# Revit family: 46-PORTARROLLOS METÁLICO
name_source: partatom
category: Aparatos sanitarios
revit_build: Autodesk Revit 2018 (Build: 20170223_1515(x64)
units: mm (PartAtom-declared; Revit-internal decimal feet)

## family parameters
Anfitrión = Cara
Compartido = No
Corte con vacíos al cargar = No
Cota de conector redondo = Diámetro de uso
Número OmniClass = 23.45.00.00
Punto de cálculo de habitación = No
Tipo de pieza = Normal
Título OmniClass = Sanitary, Laundry, and Cleaning Equipment

## types (1)
- 46-PORTARROLLOS METÁLICO
    Acabado = Brillante
    Altura Nominal = 265
    Ancho Nominal = 130
    Características = Tamaño adecuado para diferentes tamaños de rollo, sistema de fijación externa, ideal para instituciones de alto tráfico
    Color = Satinado
    Cumplimiento de Norma = Cumple con norma IAPMO IGC 157
    Código de montaje = D2010
    Descripción = Plumbing Fixtures
    Descripción IFC = Portarrollo metálico
    Descripción de la garantía = Garantía de 1 año, garantía de 3 años en acabados.
    Duración Garantía Partes = 1
    Duración Garantía Unidad = Año
    Elevación por defecto = 0 mm  [stored 0 ft]
    Fabricante = www.corona.com.co
    Forma = Cilíndrica
    Logitud Nominal = 264
    Material Acabado = Acero Inoxidable Corona
    Material de Fabricación = Acero Inoxidable
    Nombre = Portarrollo
    Nombre del Fabricante = Corona
    Número Modelo = 706670001
    Requerimientos Accesibilidad = Manual
    Responsable Garantías Partes = www.corona.com.co
    Tamaño = 265 x 130 x 265
    Tipo de Activo = Fijo
    Tráfico = Institucional

note: [stored X ft] marks values corroborated as IEEE doubles in the binary element streams (Revit-internal decimal feet)

## geometry (parser evidence)
native form markers: Sweep x2
no freeform markers — native parametric forms only
